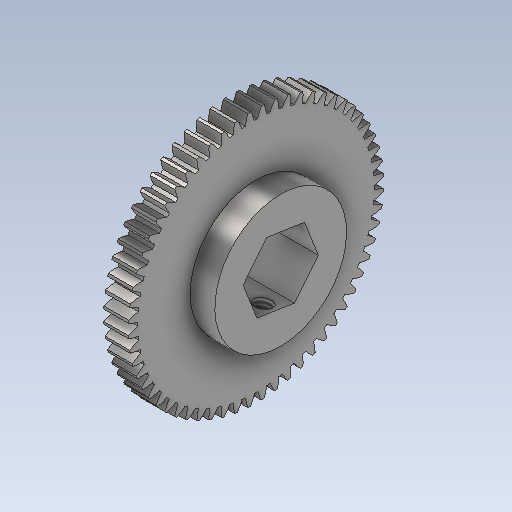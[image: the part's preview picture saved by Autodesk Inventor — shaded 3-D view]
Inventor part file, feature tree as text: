
AUTODESK INVENTOR PART (.ipt)
format: ipt  version: 2023 (Build 270158000, 158)  size: 510,464 bytes
history: native  units: in
note: dims shown in document units (in); Inventor stores cm internally (conversion verified against a paired STEP export)
features: other x3, sketch x3
ambient origin geometry x8: Origin, YZ Plane, XZ Plane, XY Plane, X Axis, Y Axis, Z Axis, Center Point
bodies: Solid1 (feature_tree)
feature tree (6):
  other  "CH-1-01-60T_Output.ipt"
  other  "Solid1::CH-1-01-60T_Output.ipt"
  other  "TaggingFeature1"
  sketch  "Sketch7"
  sketch  "Sketch6"  dims[d0=0.3937in]
  sketch  "Sketch8"
